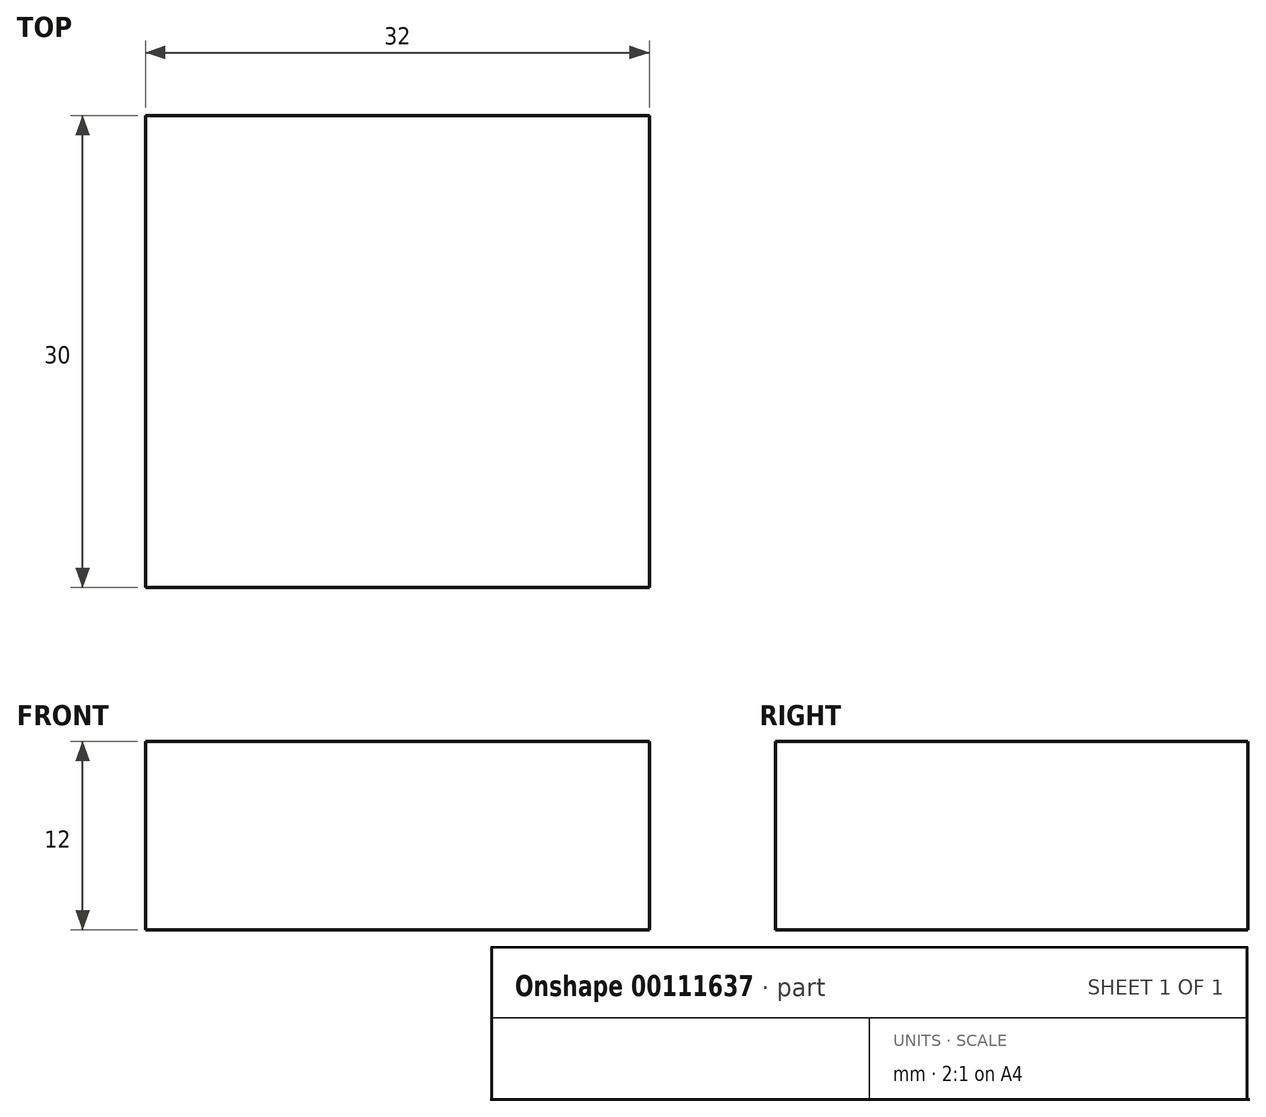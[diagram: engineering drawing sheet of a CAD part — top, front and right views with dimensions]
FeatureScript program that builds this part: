
annotation { "Feature Type Name" : "Feature", "Feature Type Description" : "" }
export const myFeature = defineFeature(function(context is Context, id is Id, definition is map)
    precondition{}
    {
        {
            var Q0;
            Q0=qCreatedBy(makeId("Front.planeOp"),FACE);
            var sketch = newSketch(context, id + "F0", { "sketchPlane" : qUnion([Q0])});
            skLineSegment(sketch, "E0.bottom", {"start": v(16, -6) * mm, "end": v(-16, -6) * mm});
            skLineSegment(sketch, "E0.top", {"start": v(16, 6) * mm, "end": v(-16, 6) * mm});
            skLineSegment(sketch, "E0.left", {"start": v(16, -6) * mm, "end": v(16, 6) * mm});
            skLineSegment(sketch, "E0.right", {"start": v(-16, -6) * mm, "end": v(-16, 6) * mm});
            skPoint(sketch, "E0.middle", {"position": v(0, 0) * mm});
            skSolve(sketch);
        }
        {
            var Q0;
            Q0 = qSketchRegion(id + "F0", true);
            extrude(context, id + "F1", {"entities" : qUnion([Q0]), "depth" : 30 * mm});
        }
    });
